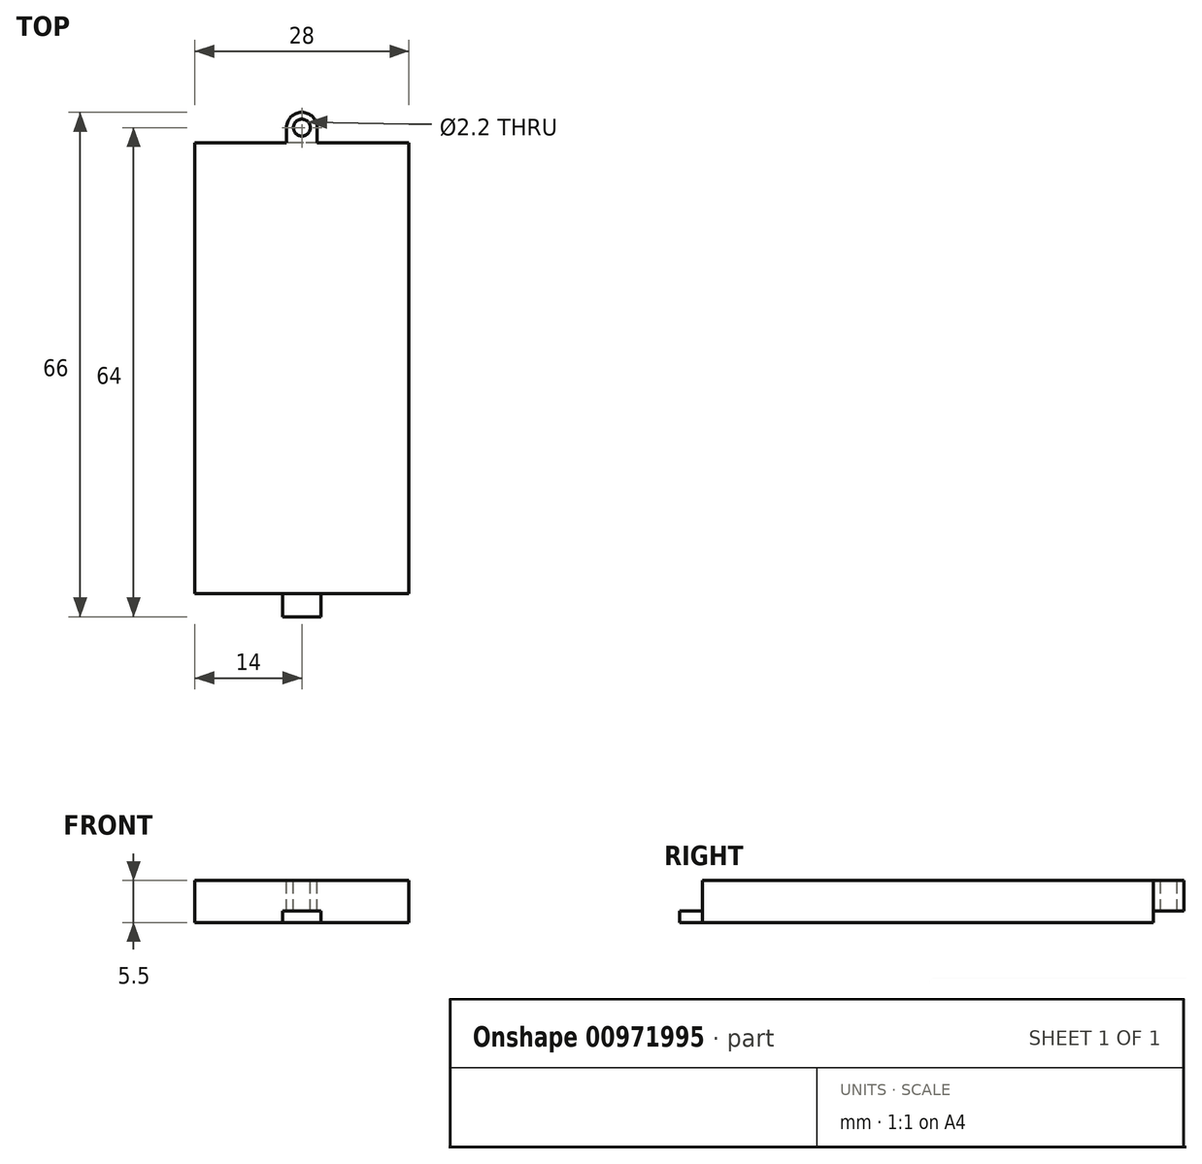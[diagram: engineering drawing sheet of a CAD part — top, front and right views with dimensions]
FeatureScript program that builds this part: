
annotation { "Feature Type Name" : "Feature", "Feature Type Description" : "" }
export const myFeature = defineFeature(function(context is Context, id is Id, definition is map)
    precondition{}
    {
        {
            var Q0;
            Q0=qCreatedBy(makeId("Top.planeOp"),FACE);
            var sketch = newSketch(context, id + "F0", { "sketchPlane" : qUnion([Q0])});
            skLineSegment(sketch, "E0.bottom", {"start": v(14, -29.5) * mm, "end": v(-14, -29.5) * mm});
            skLineSegment(sketch, "E0.top", {"start": v(14, 29.5) * mm, "end": v(-14, 29.5) * mm});
            skLineSegment(sketch, "E0.left", {"start": v(14, -29.5) * mm, "end": v(14, 29.5) * mm});
            skLineSegment(sketch, "E0.right", {"start": v(-14, -29.5) * mm, "end": v(-14, 29.5) * mm});
            skPoint(sketch, "E0.middle", {"position": v(0, 0) * mm});
            skSolve(sketch);
        }
        {
            var Q0;
            Q0 = qSketchRegion(id + "F0", true);
            extrude(context, id + "F1", {"entities" : qUnion([Q0]), "depth" : 5.5 * mm, "offsetDistance" : 25 * mm});
        }
        {
            var Q0;
            Q0=qCreatedBy(makeId("Top.planeOp"),FACE);
            var sketch = newSketch(context, id + "F2", { "sketchPlane" : qUnion([Q0])});
            skLineSegment(sketch, "E1.bottom", {"start": v(-2.5, -29.5) * mm, "end": v(2.5, -29.5) * mm});
            skLineSegment(sketch, "E1.top", {"start": v(-2.5, -32.5) * mm, "end": v(2.5, -32.5) * mm});
            skLineSegment(sketch, "E1.left", {"start": v(-2.5, -29.5) * mm, "end": v(-2.5, -32.5) * mm});
            skLineSegment(sketch, "E1.right", {"start": v(2.5, -29.5) * mm, "end": v(2.5, -32.5) * mm});
            skSolve(sketch);
        }
        {
            var Q0;
            Q0 = qSketchRegion(id + "F2", true);
            extrude(context, id + "F3", {"entities" : qUnion([Q0]), "operationType" : NewBodyOperationType.ADD, "depth" : 1.5 * mm, "offsetDistance" : 25 * mm});
        }
        {
            var Q0;
            Q0=makeQuery(id+"F1.opExtrude","CAP_FACE",FACE,{"disambiguationData":[OSD([sQuery(id+"F0.wireOp",EDGE,"E0.bottom"),sQuery(id+"F0.wireOp",EDGE,"E0.top"),sQuery(id+"F0.wireOp",EDGE,"E0.left"),sQuery(id+"F0.wireOp",EDGE,"E0.right")])],"isStart":false});
            var sketch = newSketch(context, id + "F4", { "sketchPlane" : qUnion([Q0])});
            skLineSegment(sketch, "E2.bottom", {"start": v(-2, 29.5) * mm, "end": v(2, 29.5) * mm});
            skLineSegment(sketch, "E2.top", {"start": v(-2, 31.5) * mm, "end": v(2, 31.5) * mm});
            skLineSegment(sketch, "E2.left", {"start": v(-2, 29.5) * mm, "end": v(-2, 31.5) * mm});
            skLineSegment(sketch, "E2.right", {"start": v(2, 29.5) * mm, "end": v(2, 31.5) * mm});
            skArc(sketch, "E3", {"start": v(2, 31.5) * mm, "mid": v(0, 33.5) * mm, "end": v(-2, 31.5) * mm});
            skSolve(sketch);
        }
        {
            var Q0;
            Q0 = qSketchRegion(id + "F4", true);
            extrude(context, id + "F5", {"entities" : qUnion([Q0]), "operationType" : NewBodyOperationType.ADD, "oppositeDirection" : true, "depth" : 4 * mm, "offsetDistance" : 25 * mm});
        }
        {
            var Q0;
            Q0=sQuery(id+"F4.wireOp",VERTEX,"E3.center");
            var Q1;
            Q1=makeQuery(id+"F1.opExtrude","SWEPT_BODY",BODY,{"disambiguationData":[OSD([sQuery(id+"F0.wireOp",EDGE,"E0.bottom"),sQuery(id+"F0.wireOp",EDGE,"E0.top"),sQuery(id+"F0.wireOp",EDGE,"E0.left"),sQuery(id+"F0.wireOp",EDGE,"E0.right")])]});
            hole(context, id + "F6", {"style" : HoleStyle.SIMPLE, "endStyle" : HoleEndStyle.BLIND, "holeDiameter" : 2.2 * mm, "majorDiameter" : 5 * mm, "holeDepth" : 5 * mm, "isTappedThrough" : true, "tappedDepth" : 12 * mm, "tapClearance" : 3, "locations" : qUnion([Q0]), "scope" : qUnion([Q1])});
        }
    });
